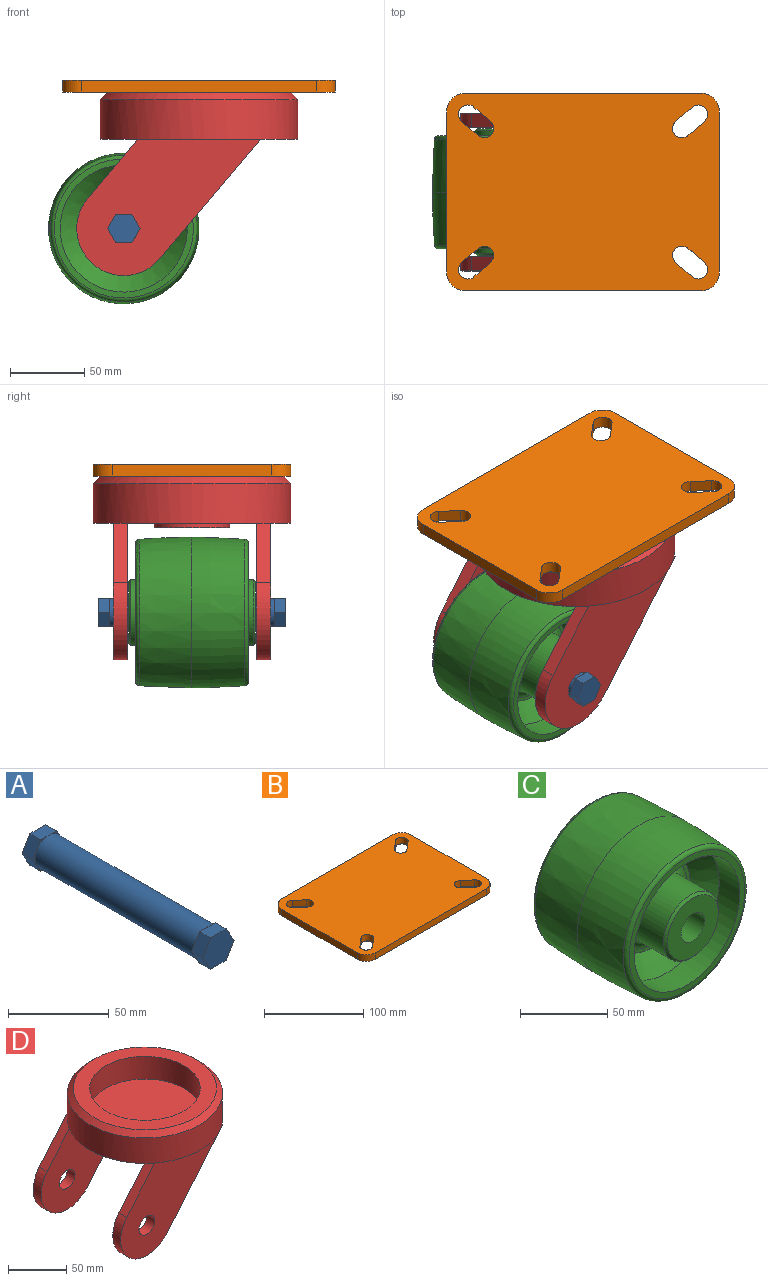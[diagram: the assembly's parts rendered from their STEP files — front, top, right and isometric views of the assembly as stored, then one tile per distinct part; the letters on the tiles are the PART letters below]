
ASSEMBLY  parts=4 mates=3
PART A: 17 faces, bbox 22x126.6x19.1 mm
  f0: cylinder r=9.5mm len=111.38mm, axis (0,1,0), area 6648mm2, adj f8,f16
  f1: plane 9.53x7.62mm, normal (0.87,0,0.5), area 83.8mm2, adj f2,f6,f7,f8
  f2: plane 11x7.62mm, normal (0,0,1), area 83.8mm2, adj f1,f3,f7,f8
  f3: plane 9.53x7.62mm, normal (-0.87,0,0.5), area 83.8mm2, adj f2,f4,f7,f8
  f4: plane 9.53x7.62mm, normal (-0.87,0,-0.5), area 83.8mm2, adj f3,f5,f7,f8
  f5: plane 11x7.62mm, normal (0,0,-1), area 83.8mm2, adj f4,f6,f7,f8
  f6: plane 9.53x7.62mm, normal (0.87,0,-0.5), area 83.8mm2, adj f1,f5,f7,f8
  f7: plane 22x19.05mm, normal (0,-1,0), area 314.3mm2, adj f1,f2,f3,f4,f5,f6
  f8: plane 22x19.05mm, normal (0,1,0), area 30.8mm2, adj f0,f1,f2,f3,f4,f5,f6
  f9: plane 9.53x7.62mm, normal (0.87,0,0.5), area 83.8mm2, adj f10,f14,f15,f16
  f10: plane 11x7.62mm, normal (0,0,1), area 83.8mm2, adj f9,f11,f15,f16
  f11: plane 9.53x7.62mm, normal (-0.87,0,0.5), area 83.8mm2, adj f10,f12,f15,f16
  f12: plane 9.53x7.62mm, normal (-0.87,0,-0.5), area 83.8mm2, adj f11,f13,f15,f16
  f13: plane 11x7.62mm, normal (0,0,-1), area 83.8mm2, adj f12,f14,f15,f16
  f14: plane 9.53x7.62mm, normal (0.87,0,-0.5), area 83.8mm2, adj f9,f13,f15,f16
  f15: plane 22x19.05mm, normal (0,1,0), area 314.3mm2, adj f9,f10,f11,f12,f13,f14
  f16: plane 22x19.05mm, normal (0,-1,0), area 30.8mm2, adj f0,f9,f10,f11,f12,f13,f14
PART B: 31 faces, bbox 184.2x133.4x32.1 mm
  f0: plane 34.29x34.29mm, normal (0,0,-1), area 923.5mm2, adj f9
  f1: plane 107.95x7.94mm, normal (-1,0,0), area 856.9mm2, adj f2,f4,f19,f30
  f2: plane 184.15x133.35mm, normal (0,0,-1), area 17815.6mm2, adj f1,f3,f5,f6,f10,f11,f12,f13
  f3: plane 107.95x7.94mm, normal (1,0,0), area 856.9mm2, adj f2,f4,f18,f29
  f4: plane 184.15x133.35mm, normal (0,0,1), area 23167.7mm2, adj f1,f3,f5,f10,f11,f12,f13,f14
  f5: plane 158.75x7.94mm, normal (0,-1,0), area 1260.1mm2, adj f2,f4,f18,f19
  f6: cylinder r=41.27mm len=82.55mm, axis (0,0,1), area 6257.8mm2, adj f2,f8
  f7: cylinder r=22.23mm len=44.45mm, axis (0,0,1), area 2660.2mm2, adj f8,f9
  f8: plane 82.55x82.55mm, normal (0,0,-1), area 3800.3mm2, adj f6,f7
  f9: cone r=22.23mm half-angle=45deg, axis (0,0,-1), area 888.6mm2, adj f0,f7
  f10: cylinder r=6.35mm len=11.17mm, axis (0,0,1), area 158.3mm2, adj f2,f4,f11,f13
  f11: plane 11.11x9.53mm, normal (-0.65,0.76,0), area 116.2mm2, adj f2,f4,f10,f12
  f12: cylinder r=6.35mm len=11.17mm, axis (0,0,1), area 158.3mm2, adj f2,f4,f11,f13
  f13: plane 11.11x9.53mm, normal (0.65,-0.76,0), area 116.2mm2, adj f2,f4,f10,f12
  f14: cylinder r=6.35mm len=11.17mm, axis (0,0,1), area 158.3mm2, adj f2,f4,f15,f17
  f15: plane 11.11x9.53mm, normal (0.65,0.76,0), area 116.2mm2, adj f2,f4,f14,f16
  f16: cylinder r=6.35mm len=11.17mm, axis (0,0,1), area 158.3mm2, adj f2,f4,f15,f17
  f17: plane 11.11x9.53mm, normal (-0.65,-0.76,0), area 116.2mm2, adj f2,f4,f14,f16
  f18: cylinder r=12.7mm len=12.7mm, axis (0,0,-1), area 158.3mm2, adj f2,f3,f4,f5
  f19: cylinder r=12.7mm len=12.7mm, axis (0,0,1), area 158.3mm2, adj f1,f2,f4,f5
  f20: plane 158.75x7.94mm, normal (0,1,0), area 1260.1mm2, adj f2,f4,f29,f30
  f21: cylinder r=6.35mm len=11.17mm, axis (0,0,1), area 158.3mm2, adj f2,f4,f22,f24
  f22: plane 11.11x9.53mm, normal (-0.65,-0.76,0), area 116.2mm2, adj f2,f4,f21,f23
  f23: cylinder r=6.35mm len=11.17mm, axis (0,0,1), area 158.3mm2, adj f2,f4,f22,f24
  f24: plane 11.11x9.53mm, normal (0.65,0.76,0), area 116.2mm2, adj f2,f4,f21,f23
  f25: cylinder r=6.35mm len=11.17mm, axis (0,0,1), area 158.3mm2, adj f2,f4,f26,f28
  f26: plane 11.11x9.53mm, normal (0.65,-0.76,0), area 116.2mm2, adj f2,f4,f25,f27
  f27: cylinder r=6.35mm len=11.17mm, axis (0,0,1), area 158.3mm2, adj f2,f4,f26,f28
  f28: plane 11.11x9.53mm, normal (-0.65,0.76,0), area 116.2mm2, adj f2,f4,f25,f27
  f29: cylinder r=12.7mm len=12.7mm, axis (0,0,-1), area 158.3mm2, adj f2,f3,f4,f20
  f30: cylinder r=12.7mm len=12.7mm, axis (0,0,1), area 158.3mm2, adj f1,f2,f4,f20
PART C: 21 faces, bbox 107.1x85.7x107.1 mm
  f0: revolved ~101.6x101.6mm, area 22642.3mm2, adj f8,f19
  f1: plane 41.4x41.4mm, normal (0,-1,0), area 1061.2mm2, adj f10,f11
  f2: cylinder r=22.23mm len=44.45mm, axis (0,1,0), area 3555.8mm2, adj f3,f10
  f3: torus R=28.57mm, axis (0,1,0), area 1537.5mm2, adj f2,f4
  f4: plane 62.18x62.18mm, normal (0,-1,0), area 471.4mm2, adj f3,f5
  f5: cone r=31.09mm half-angle=45deg, axis (0,-1,0), area 3892.2mm2, adj f4,f6
  f6: cylinder r=42.93mm len=85.85mm, axis (0,1,0), area 4514.7mm2, adj f5,f7
  f7: plane 93.85x93.85mm, normal (0,-1,0), area 1129mm2, adj f6,f9
  f8: revolved ~101.6x101.6mm, area 11321.2mm2, adj f0,f9
  f9: torus R=46.93mm, axis (0,1,0), area 1157.7mm2, adj f7,f8
  f10: cone r=22.23mm half-angle=45deg, axis (0,1,0), area 290.6mm2, adj f1,f2
  f11: cylinder r=9.53mm len=85.73mm, axis (0,1,0), area 5130.4mm2, adj f1,f12
  f12: plane 41.4x41.4mm, normal (0,1,0), area 1061.2mm2, adj f11,f20
  f13: cylinder r=22.23mm len=44.45mm, axis (0,-1,0), area 3555.8mm2, adj f14,f20
  f14: torus R=28.57mm, axis (0,-1,0), area 1537.5mm2, adj f13,f15
  f15: plane 62.18x62.18mm, normal (0,1,0), area 471.4mm2, adj f14,f16
  f16: cone r=31.09mm half-angle=45deg, axis (0,1,0), area 3892.2mm2, adj f15,f17
  f17: cylinder r=42.93mm len=85.85mm, axis (0,-1,0), area 4514.7mm2, adj f16,f18
  f18: plane 93.85x93.85mm, normal (0,1,0), area 1129mm2, adj f17,f19
  f19: torus R=46.93mm, axis (0,-1,0), area 1157.7mm2, adj f0,f18
  f20: cone r=22.23mm half-angle=45deg, axis (0,-1,0), area 290.6mm2, adj f12,f13
PART D: 26 faces, bbox 149.2x133.4x123.9 mm
  f0: plane 133.35x104.36mm, normal (0,0,-1), area 8876mm2, adj f3,f5,f7,f9,f11,f19,f21,f23
  f1: plane 1.25x0.97mm, normal (0,0,1), area 0.6mm2, adj f3,f6,f9
  f2: plane 1.25x0.97mm, normal (0,0,1), area 0.6mm2, adj f5,f6,f9
  f3: plane 39.87x33.58mm, normal (-0.76,0,0.64), area 496.5mm2, adj f0,f1,f4,f6,f7
  f4: cylinder r=31.75mm len=56.04mm, axis (0,1,0), area 950.1mm2, adj f3,f5,f6,f7
  f5: plane 80.78x68.02mm, normal (0.76,0,-0.64), area 1005.9mm2, adj f0,f2,f4,f6,f7
  f6: plane 124.06x92.08mm, normal (0,-1,0), area 6306.4mm2, adj f1,f2,f3,f4,f5,f8,f16
  f7: plane 124.06x92.08mm, normal (0,1,0), area 6306.4mm2, adj f0,f3,f4,f5,f16
  f8: plane 80.52x13.53mm, normal (0,0,-1), area 742.1mm2, adj f6,f9
  f9: cylinder r=66.67mm len=133.35mm, axis (0,0,-1), area 11199.5mm2, adj f0,f1,f2,f8,f15,f17,f18,f24
  f10: plane 95.25x95.25mm, normal (0,0,1), area 7125.6mm2, adj f13
  f11: cylinder r=25.4mm len=50.8mm, axis (0,0,1), area 506.7mm2, adj f0,f12
  f12: plane 50.8x50.8mm, normal (0,0,-1), area 2026.8mm2, adj f11
  f13: cylinder r=47.62mm len=95.25mm, axis (0,0,-1), area 7144.6mm2, adj f10,f14
  f14: plane 123.19x123.19mm, normal (0,0,1), area 4793.5mm2, adj f13,f15
  f15: cone r=66.67mm half-angle=45deg, axis (0,0,-1), area 2895mm2, adj f9,f14
  f16: cylinder r=9.53mm len=19.05mm, axis (0,1,0), area 570mm2, adj f6,f7
  f17: plane 1.25x0.97mm, normal (0,0,1), area 0.6mm2, adj f9,f19,f22
  f18: plane 1.25x0.97mm, normal (0,0,1), area 0.6mm2, adj f9,f21,f22
  f19: plane 39.87x33.58mm, normal (-0.76,0,0.64), area 496.5mm2, adj f0,f17,f20,f22,f23
  f20: cylinder r=31.75mm len=56.04mm, axis (0,-1,0), area 950.1mm2, adj f19,f21,f22,f23
  f21: plane 80.78x68.02mm, normal (0.76,0,-0.64), area 1005.9mm2, adj f0,f18,f20,f22,f23
  f22: plane 124.06x92.08mm, normal (0,1,0), area 6306.4mm2, adj f17,f18,f19,f20,f21,f24,f25
  f23: plane 124.06x92.08mm, normal (0,-1,0), area 6306.4mm2, adj f0,f19,f20,f21,f25
  f24: plane 80.52x13.53mm, normal (0,0,-1), area 742.1mm2, adj f9,f22
  f25: cylinder r=9.53mm len=19.05mm, axis (0,-1,0), area 570mm2, adj f22,f23
PLACE A t=(-197.98,-71.25,-16.93)mm
PLACE B t=(-197.98,-71.25,-18.46)mm
PLACE C t=(-197.98,-71.25,-16.93)mm
PLACE D t=(-197.98,-71.25,-16.93)mm
MATE revolute A.f0 <-> D.f25  axis (0,-1,0) through (-197.98,-15.56,-16.93)mm
MATE revolute A.f0 <-> C.f5  axis (0,1,0) through (-197.98,-71.25,-16.93)mm
MATE revolute D.f9 <-> B.f9  axis (0,0,1) through (-147.18,-71.25,75.21)mm
